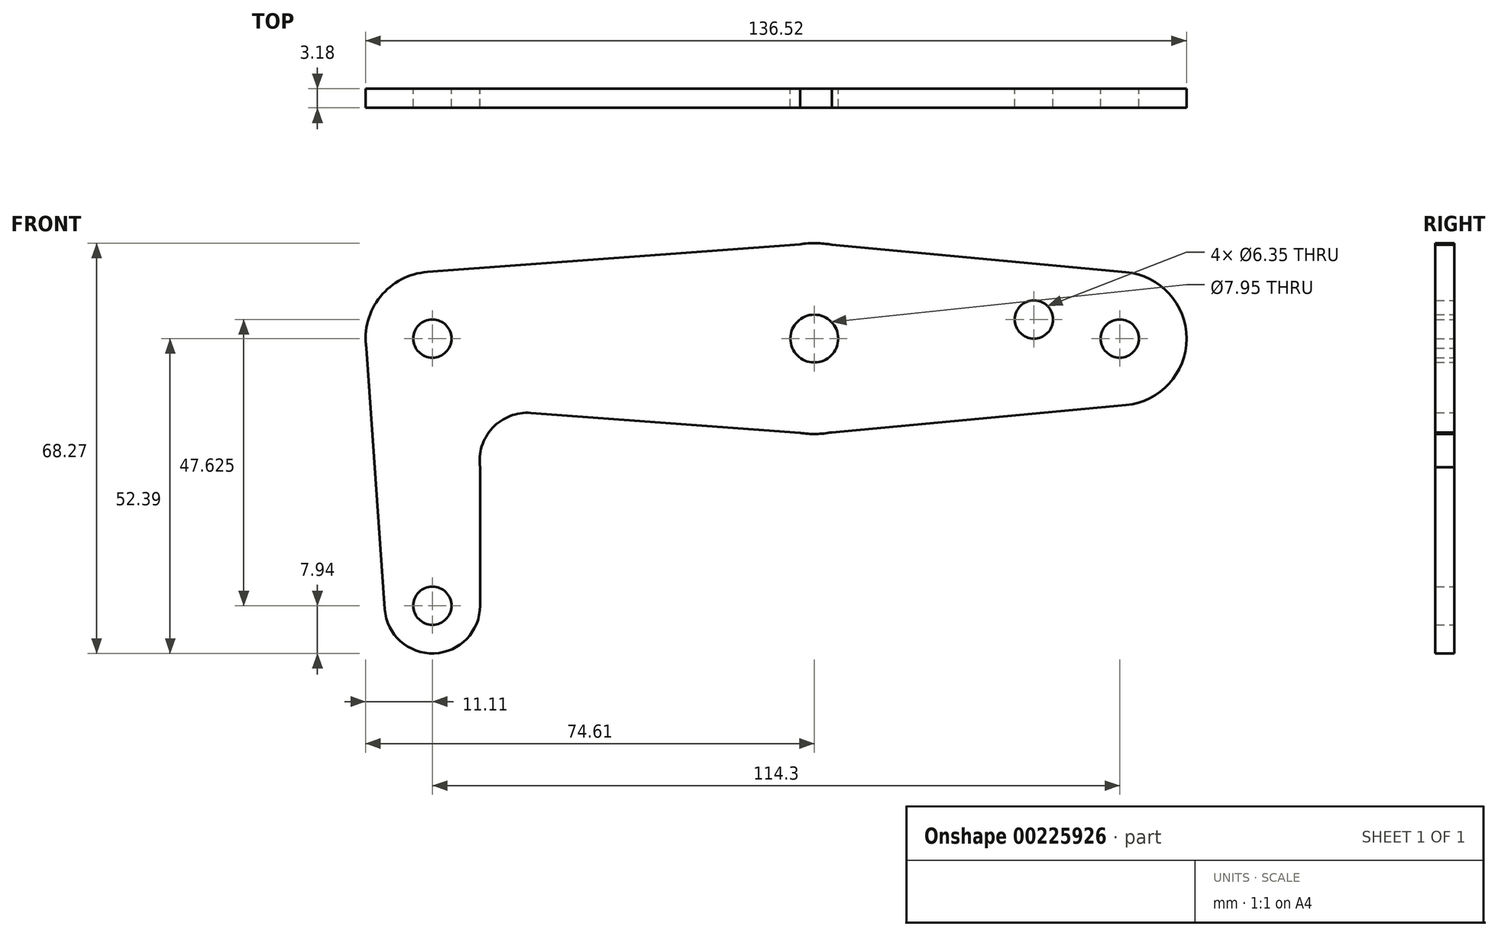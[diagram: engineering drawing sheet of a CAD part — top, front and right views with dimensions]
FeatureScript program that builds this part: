
annotation { "Feature Type Name" : "Feature", "Feature Type Description" : "" }
export const myFeature = defineFeature(function(context is Context, id is Id, definition is map)
    precondition{}
    {
        {
            var Q0;
            Q0=qCreatedBy(makeId("Front.planeOp"),FACE);
            var sketch = newSketch(context, id + "F0", { "sketchPlane" : qUnion([Q0])});
            skCircle(sketch, "E0", {"center": v(0, 0) * mm, "radius": 15.88 * mm});
            skCircle(sketch, "E1", {"center": v(0, 0) * mm, "radius": 3.98 * mm});
            skCircle(sketch, "E2", {"center": v(0, 0) * mm, "radius": 3.18 * mm});
            skLineSegment(sketch, "E3", {"start": v(0, 0) * mm, "end": v(-63.5, 0) * mm, "construction": true});
            skLineSegment(sketch, "E4", {"start": v(0, 0) * mm, "end": v(50.8, 0) * mm, "construction": true});
            skCircle(sketch, "E5", {"center": v(-63.5, 0) * mm, "radius": 11.11 * mm});
            skCircle(sketch, "E6", {"center": v(50.8, 0) * mm, "radius": 11.11 * mm});
            skCircle(sketch, "E7", {"center": v(-63.5, 0) * mm, "radius": 3.18 * mm});
            skCircle(sketch, "E8", {"center": v(50.8, 0) * mm, "radius": 3.18 * mm});
            skLineSegment(sketch, "E9", {"start": v(-63.5, 0) * mm, "end": v(-63.5, -44.45) * mm, "construction": true});
            skCircle(sketch, "E10", {"center": v(-63.5, -44.45) * mm, "radius": 7.94 * mm});
            skCircle(sketch, "E11", {"center": v(-63.5, -44.45) * mm, "radius": 3.18 * mm});
            skCircle(sketch, "E12", {"center": v(36.53, 3.18) * mm, "radius": 3.18 * mm});
            skLineSegment(sketch, "E13", {"start": v(0, 15.88) * mm, "end": v(-64.33, 11.08) * mm});
            skLineSegment(sketch, "E14", {"start": v(0, -15.88) * mm, "end": v(-47.1, -12.37) * mm});
            skLineSegment(sketch, "E15", {"start": v(0, -15.88) * mm, "end": v(51.83, -11.06) * mm});
            skLineSegment(sketch, "E16", {"start": v(0, 15.88) * mm, "end": v(51.83, 11.06) * mm});
            skLineSegment(sketch, "E17", {"start": v(-74.61, 0) * mm, "end": v(-71.42, -45.01) * mm});
            skLineSegment(sketch, "E18", {"start": v(-55.56, -44.45) * mm, "end": v(-55.56, -21.43) * mm});
            skArc(sketch, "E19", {"start": v(-47.1, -12.37) * mm, "mid": v(-53.5, -14.87) * mm, "end": v(-55.56, -21.43) * mm});
            skSolve(sketch);
        }
        {
            var Q0;
            Q0 = qSketchRegion(id + "F0", true);
            extrude(context, id + "F1", {"entities" : qUnion([Q0]), "depth" : 3.17 * mm});
        }
    });
